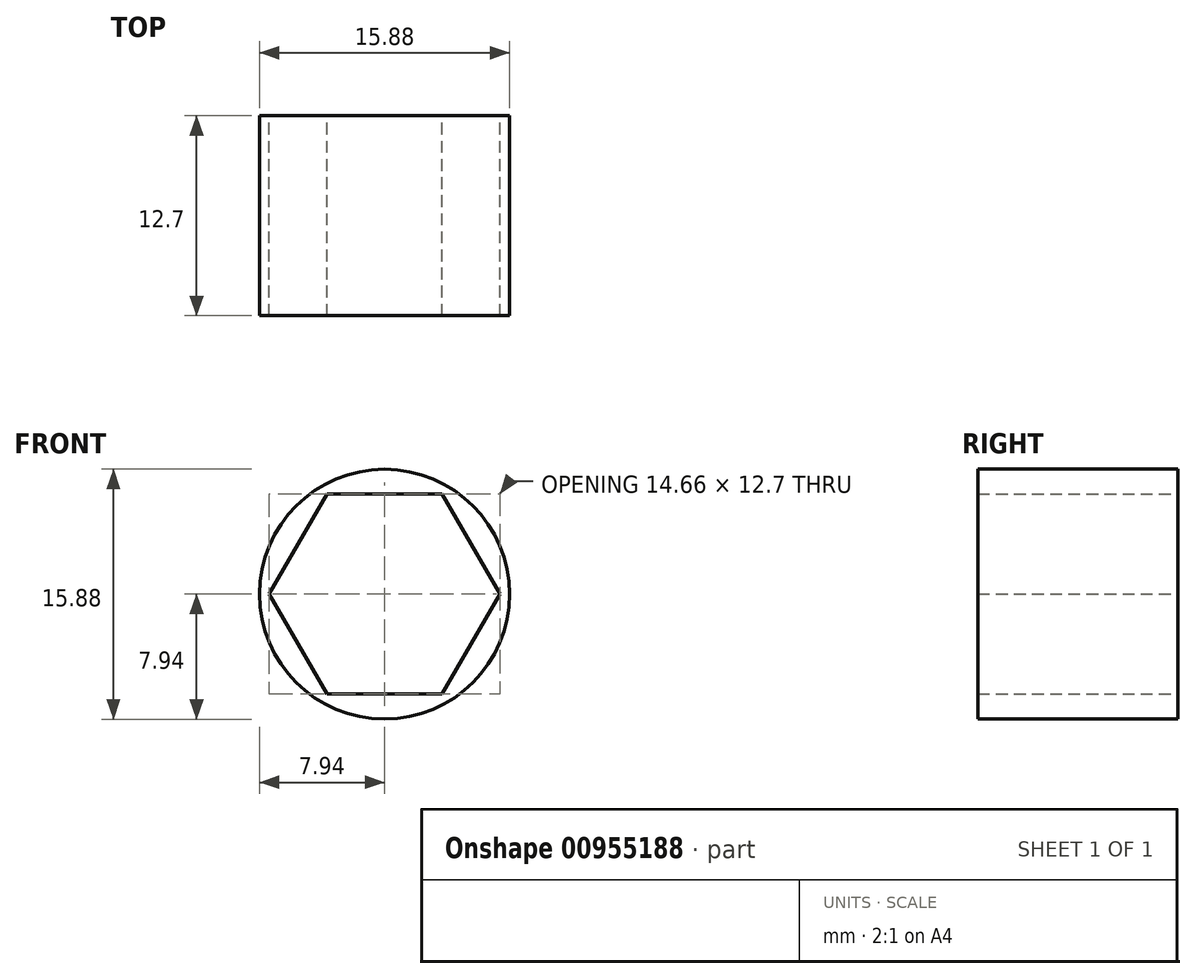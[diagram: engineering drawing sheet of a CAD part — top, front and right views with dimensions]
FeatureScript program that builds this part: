
annotation { "Feature Type Name" : "Feature", "Feature Type Description" : "" }
export const myFeature = defineFeature(function(context is Context, id is Id, definition is map)
    precondition{}
    {
        {
            var Q0;
            Q0=qCreatedBy(makeId("Front.planeOp"),FACE);
            var sketch = newSketch(context, id + "F0", { "sketchPlane" : qUnion([Q0])});
            skCircle(sketch, "E0", {"center": v(0, 0) * mm, "radius": 7.94 * mm});
            skCircle(sketch, "E1.cCircle", {"center": v(0, 0) * mm, "radius": 6.35 * mm, "construction": true});
            skLineSegment(sketch, "E1.0", {"start": v(-3.67, 6.35) * mm, "end": v(3.67, 6.35) * mm});
            skLineSegment(sketch, "E1.1", {"start": v(3.67, 6.35) * mm, "end": v(7.33, 0) * mm});
            skLineSegment(sketch, "E1.2", {"start": v(7.33, 0) * mm, "end": v(3.67, -6.35) * mm});
            skLineSegment(sketch, "E1.3", {"start": v(3.67, -6.35) * mm, "end": v(-3.67, -6.35) * mm});
            skLineSegment(sketch, "E1.4", {"start": v(-3.67, -6.35) * mm, "end": v(-7.33, 0) * mm});
            skLineSegment(sketch, "E1.5", {"start": v(-7.33, 0) * mm, "end": v(-3.67, 6.35) * mm});
            skPoint(sketch, "E1.0.midPoint", {"position": v(0, 6.35) * mm});
            skSolve(sketch);
        }
        {
            var Q0;
            Q0=qSketchRegion(id+"F0",true);
            extrude(context, id + "F1", {"entities" : qUnion([Q0]), "depth" : 12.7 * mm, "offsetDistance" : 25.4 * mm});
        }
    });
